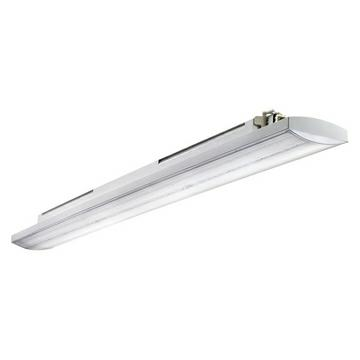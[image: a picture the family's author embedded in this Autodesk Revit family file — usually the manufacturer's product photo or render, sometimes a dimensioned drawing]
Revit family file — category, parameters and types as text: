
# Revit family: Lighting-Industriale-GEWISS-SMART[3]PLUS-HLO-PLAFONIERA-LED-EMERGENZA_TRANSPARENTE_1600mm
name_source: partatom
category: Apparecchi per illuminazione
units: mm (PartAtom-declared; Revit-internal decimal feet)

## family parameters
Condiviso = No
Host = Superficie
Punto di calcolo locali = No
Quota connettore circolare = Usa diametro
Sorgente d'illuminazione = No
Taglio con vuoti quando caricato = No
Tipo di parte = Normale

## types (1)
- Lighting-Industriale-GEWISS-SMART[3]PLUS-HLO-PLAFONIERA-LED-EMERGENZA_TRANSPARENTE_1600mm
    Applicazione = Interno
    Carico apparente = 26 VA
    Catalogo = LIGHTING
    Catalogo Serie = SMART[3] PLUS HLO
    Classe di efficienza LED integrati = A ÷ A++
    Classe isolamento = II
    Codice Electrocod = 2434
    Commenti sul wattaggio = 26W
    Descrizione = SMART3 PLUS 1600 EMERG DT1+DT6 HO TRASP 9 57
    Ganci = Alluminio
    Garanzia = ND
    Glow Wire Test = 850°C
    Grado di protezione = IP66/IP69
    IDF = 20be86eb-b235-424b-90a6-5190a60e8883
    IDT = 0d0c36dd-7d20-424d-bc0a-e9538265b617
    Immagine tipo = GWS3158TL.jpg
    Lampada = LED
    Lampada: = LED
    Lumen output (lm) = 7400
    Lunghezza = 1600 mm
    Lunghezza Lampada = 1600 mm
    Modello = GWS3325BT957
    Numero poli = 2
    Potenza di sistema = 50 W
    Produttore = GEWISS S.p.A.
    Prospetto di default = 1219 mm
    Resistenza agli urti = IK08
    SEO = Plafoniera
    Scheda Tecnica = https://www.gewiss.com
    Schermo = Trasparente
    Schermo. = Led Acceso
    Stampa 1_100 = Sì
    Stampa 1_200 = No
    Struttura = GRIGIO
    Temperatura di colore = 5700 K (CRI > 90)
    Temperatura di colore: = 5700 K (CRI > 90)
    Temperatura di funzionamento = ND
    Temperatura di utilizzo = ND
    Tensione = 220-240 V
    Tipologia sorgente luminosa = LED - Non sostituibile
    URL = https://www.gewiss.com
    Versione file RFA = 20.0
